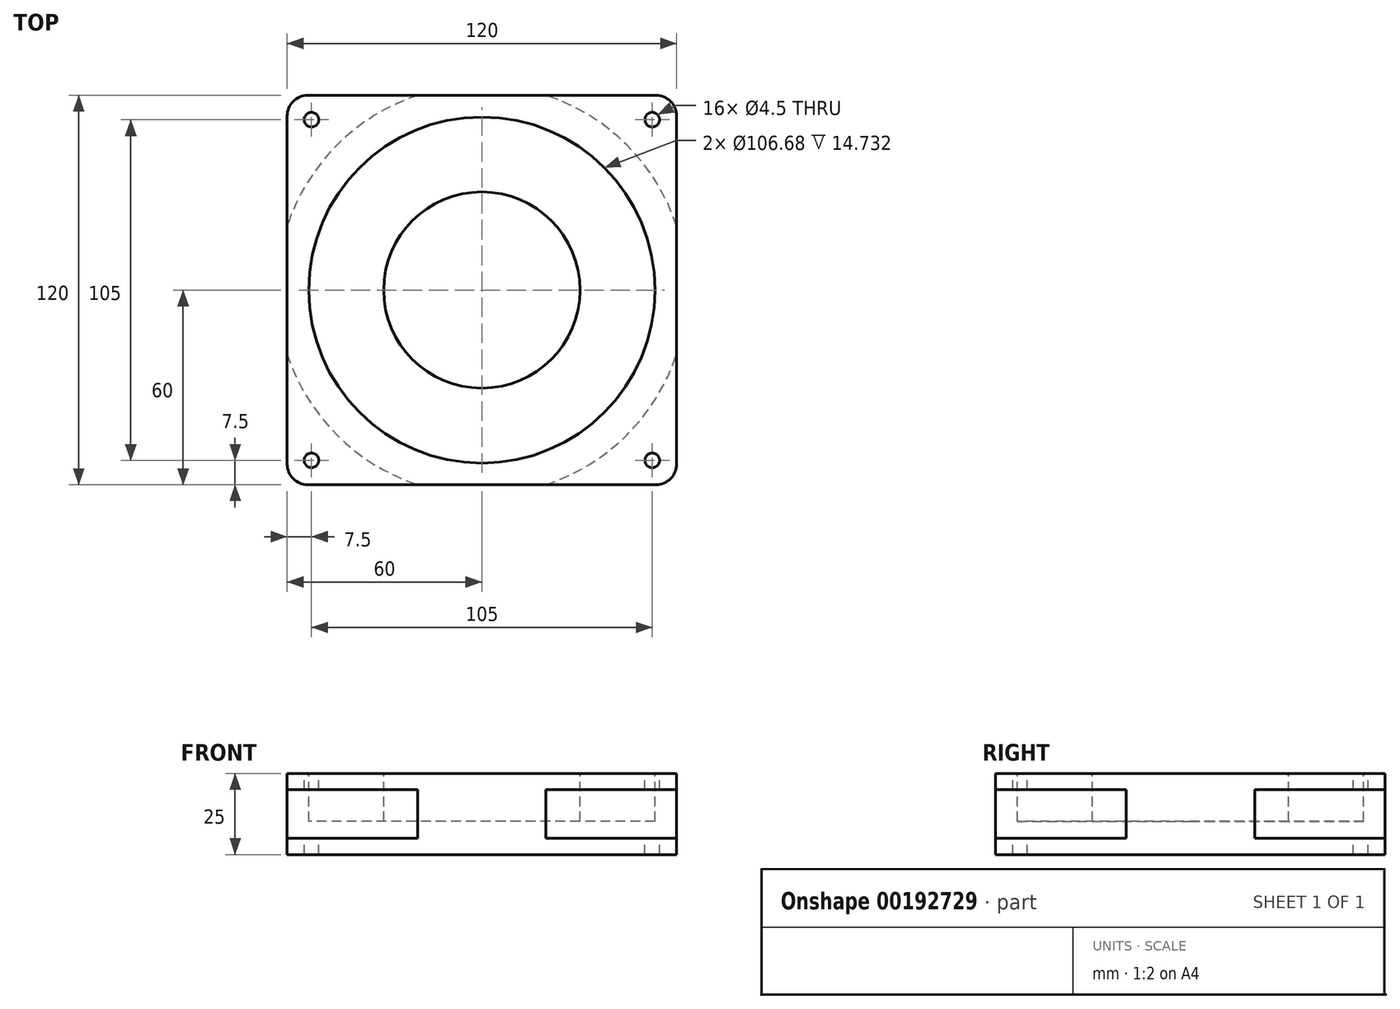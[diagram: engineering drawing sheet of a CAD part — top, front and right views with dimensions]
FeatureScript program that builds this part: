
annotation { "Feature Type Name" : "Feature", "Feature Type Description" : "" }
export const myFeature = defineFeature(function(context is Context, id is Id, definition is map)
    precondition{}
    {
        {
            var Q0;
            Q0=qCreatedBy(makeId("Top.planeOp"),FACE);
            var sketch = newSketch(context, id + "F0", { "sketchPlane" : qUnion([Q0])});
            skLineSegment(sketch, "E0.bottom", {"start": v(60, 60) * mm, "end": v(-60, 60) * mm});
            skLineSegment(sketch, "E0.top", {"start": v(60, -60) * mm, "end": v(-60, -60) * mm});
            skLineSegment(sketch, "E0.left", {"start": v(60, 60) * mm, "end": v(60, -60) * mm});
            skLineSegment(sketch, "E0.right", {"start": v(-60, 60) * mm, "end": v(-60, -60) * mm});
            skPoint(sketch, "E0.middle", {"position": v(0, 0) * mm});
            skSolve(sketch);
        }
        {
            var Q0;
            Q0 = qSketchRegion(id + "F0", true);
            extrude(context, id + "F1", {"entities" : qUnion([Q0]), "oppositeDirection" : true, "depth" : 25 * mm});
        }
        {
            var Q0;
            Q0=makeQuery(id+"F1.opExtrude","CAP_FACE",FACE,{"disambiguationData":[OSD([sQuery(id+"F0.wireOp",EDGE,"E0.bottom"),sQuery(id+"F0.wireOp",EDGE,"E0.top"),sQuery(id+"F0.wireOp",EDGE,"E0.left"),sQuery(id+"F0.wireOp",EDGE,"E0.right")])],"isStart":true});
            var sketch = newSketch(context, id + "F2", { "sketchPlane" : qUnion([Q0])});
            skPoint(sketch, "E1", {"position": v(-52.5, -52.5) * mm});
            skPoint(sketch, "E2", {"position": v(-52.5, 52.5) * mm});
            skPoint(sketch, "E3", {"position": v(52.5, 52.5) * mm});
            skPoint(sketch, "E4", {"position": v(52.5, -52.5) * mm});
            skLineSegment(sketch, "E5", {"start": v(-60, 0) * mm, "end": v(60, 0) * mm, "construction": true});
            skLineSegment(sketch, "E6", {"start": v(0, 60) * mm, "end": v(0, -60) * mm, "construction": true});
            skSolve(sketch);
        }
        {
            var Q0;
            Q0=sQuery(id+"F2.wireOp",VERTEX,"E1");
            var Q1;
            Q1=sQuery(id+"F2.wireOp",VERTEX,"E4");
            var Q2;
            Q2=sQuery(id+"F2.wireOp",VERTEX,"E3");
            var Q3;
            Q3=sQuery(id+"F2.wireOp",VERTEX,"E2");
            var Q4;
            Q4=makeQuery(id+"F1.opExtrude","SWEPT_BODY",BODY,{"disambiguationData":[OSD([sQuery(id+"F0.wireOp",EDGE,"E0.bottom"),sQuery(id+"F0.wireOp",EDGE,"E0.top"),sQuery(id+"F0.wireOp",EDGE,"E0.left"),sQuery(id+"F0.wireOp",EDGE,"E0.right")])]});
            hole(context, id + "F3", {"style" : HoleStyle.SIMPLE, "endStyle" : HoleEndStyle.THROUGH, "holeDiameter" : 4.5 * mm, "locations" : qUnion([Q0, Q1, Q2, Q3]), "scope" : qUnion([Q4]), "isTappedThrough" : true});
        }
        {
            var Q0;
            Q0=makeQuery(id+"F1.opExtrude","CAP_FACE",FACE,{"disambiguationData":[OSD([sQuery(id+"F0.wireOp",EDGE,"E0.bottom"),sQuery(id+"F0.wireOp",EDGE,"E0.top"),sQuery(id+"F0.wireOp",EDGE,"E0.left"),sQuery(id+"F0.wireOp",EDGE,"E0.right")])],"isStart":true});
            var sketch = newSketch(context, id + "F4", { "sketchPlane" : qUnion([Q0])});
            skCircle(sketch, "E7", {"center": v(0, 0) * mm, "radius": 30.25 * mm});
            skCircle(sketch, "E8", {"center": v(0, 0) * mm, "radius": 53.34 * mm});
            skSolve(sketch);
        }
        {
            var Q0;
            Q0=makeQuery(id+"F4.imprint","IMPRINT",FACE,{"disambiguationData":[TD([[makeQuery(id+"F4.imprint","IMPRINT",EDGE,{"derivedFrom":sQuery(id+"F4.wireOp",EDGE,"E7")}),-1.0]])]});
            extrude(context, id + "F5", {"entities" : qUnion([Q0]), "operationType" : NewBodyOperationType.REMOVE, "oppositeDirection" : true, "depth" : 14.73 * mm});
        }
        {
            var Q0;
            Q0=makeQuery(id+"F1.opExtrude","SWEPT_EDGE",EDGE,{"disambiguationData":[OSD([sQuery(id+"F0.wireOp",EDGE,"E0.top"),sQuery(id+"F0.wireOp",EDGE,"E0.left")])]});
            var Q1;
            Q1=makeQuery(id+"F1.opExtrude","SWEPT_EDGE",EDGE,{"disambiguationData":[OSD([sQuery(id+"F0.wireOp",EDGE,"E0.top"),sQuery(id+"F0.wireOp",EDGE,"E0.right")])]});
            var Q2;
            Q2=makeQuery(id+"F1.opExtrude","SWEPT_EDGE",EDGE,{"disambiguationData":[OSD([sQuery(id+"F0.wireOp",EDGE,"E0.bottom"),sQuery(id+"F0.wireOp",EDGE,"E0.left")])]});
            var Q3;
            Q3=makeQuery(id+"F1.opExtrude","SWEPT_EDGE",EDGE,{"disambiguationData":[OSD([sQuery(id+"F0.wireOp",EDGE,"E0.bottom"),sQuery(id+"F0.wireOp",EDGE,"E0.right")])]});
            fillet(context, id + "F6", {"entities" : qUnion([Q0, Q1, Q2, Q3]), "radius" : 6.35 * mm, "tangentPropagation" : true, "allowEdgeOverflow" : false});
        }
        {
            var Q0;
            {var subQ0=sQuery(id+"F0.wireOp",EDGE,"E0.left");var subQ1=sQuery(id+"F0.wireOp",EDGE,"E0.top");Q0=makeQuery(id+"F6.opFillet","BLEND_EDGE",EDGE,{"blendedFrom":[makeQuery(id+"F1.opExtrude","SWEPT_EDGE",EDGE,{"disambiguationData":[OSD([subQ1,subQ0])]}),makeQuery(id+"F1.opExtrude","CAP_FACE",FACE,{"disambiguationData":[OSD([sQuery(id+"F0.wireOp",EDGE,"E0.bottom"),subQ1,subQ0,sQuery(id+"F0.wireOp",EDGE,"E0.right")])],"isStart":false})],"blendedInto":[makeQuery(id+"F1.opExtrude","CAP_FACE",FACE,{"disambiguationData":[OSD([sQuery(id+"F0.wireOp",EDGE,"E0.bottom"),subQ1,subQ0,sQuery(id+"F0.wireOp",EDGE,"E0.right")])],"isStart":false})]});}
            cPoint(context, id + "F7", {"entities" : qUnion([Q0]), "parameter" : 0.5});
        }
        {
            var Q0;
            Q0 = qCreatedBy(id + "F7" ,VERTEX);
            var Q1;
            Q1=makeQuery(id+"F5.boolean.opBoolean","COPY",EDGE,{"derivedFrom":makeQuery(id+"F5.opExtrude","CAP_EDGE",EDGE,{"disambiguationData":[OSD([sQuery(id+"F4.wireOp",EDGE,"E7")])],"isStart":true})});
            cPlane(context, id + "F8", {"entities" : qUnion([Q0, Q1]), "cplaneType" : CPlaneType.CURVE_POINT, "offset" : 25.4 * mm, "width" : 152.4 * mm, "height" : 152.4 * mm});
        }
        {
            var Q0;
            Q0=qCreatedBy(id+"F8.planeOp",FACE);
            var sketch = newSketch(context, id + "F9", { "sketchPlane" : qUnion([Q0])});
            skLineSegment(sketch, "E9.bottom", {"start": v(-63.17, -5) * mm, "end": v(-82.22, -5) * mm});
            skLineSegment(sketch, "E9.top", {"start": v(-63.17, -20) * mm, "end": v(-82.22, -20) * mm});
            skLineSegment(sketch, "E9.left", {"start": v(-63.17, -5) * mm, "end": v(-63.17, -20) * mm});
            skLineSegment(sketch, "E9.right", {"start": v(-82.22, -5) * mm, "end": v(-82.22, -20) * mm});
            skLineSegment(sketch, "E10", {"start": v(-82.22, -25) * mm, "end": v(-82.22, 0) * mm});
            skSolve(sketch);
        }
        {
            var Q0;
            Q0 = qSketchRegion(id + "F9", true);
            var Q1;
            Q1=makeQuery(id+"F5.boolean.opBoolean","COPY",EDGE,{"derivedFrom":makeQuery(id+"F5.opExtrude","CAP_EDGE",EDGE,{"disambiguationData":[OSD([sQuery(id+"F4.wireOp",EDGE,"E7")])],"isStart":true})});
            revolve(context, id + "F10", {"operationType" : NewBodyOperationType.REMOVE, "entities" : qUnion([Q0]), "axis" : qUnion([Q1]), "revolveType" : RevolveType.FULL, "oppositeDirection" : true});
        }
    });
